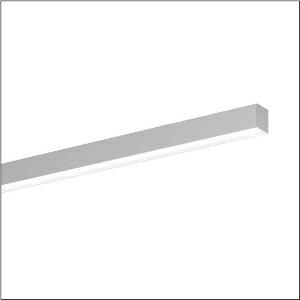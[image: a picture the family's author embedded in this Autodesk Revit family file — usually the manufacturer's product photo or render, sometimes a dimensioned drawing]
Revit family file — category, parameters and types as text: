
# Revit family: silica_r__21_51mx20tat2s_7558
name_source: partatom
category: Lighting Fixtures
units: mm (PartAtom-declared; Revit-internal decimal feet)

## family parameters
Cut with Voids When Loaded = No
Host = Face
Light Source = No
Part Type = Normal
Room Calculation Point = No
Round Connector Dimension = Use Diameter
Shared = No

## types (1)
- --- (1 x LED, 2400 lm, 20.5 W, 6500K)
    Apparent Load = 21 VA
    CIE Flux Codes = 48 79 96 100 100
    Color Rendering = 80
    Color Temperature = 6500K
    Default Elevation = 1800 mm
    Description = Silica® 21, office luminaire, primary optical cover: cover, of PMMA, opal, light emission: direct distribution, primary light characteristic: symmetric, installation type: surface-mounted, LED, rated luminous flux: 2.400lm, luminous efficacy: 112lm/W, light colour: 8tw, colour temperature: 2700..6500K, control gear: ECG DALI, with terminal, 3+2-pole, max. 2.5mm², mains connection: 220..240V, AC, 50/60Hz, rated input power: 21.5W, luminaire housing, of aluminium, metallic grey (RAL 9006), length: 1.204mm, width: 53mm, height: 53mm, protection rating (complete): IP20, insulation class (complete): insulation class I (protective earthing), certification: CE, permissible operating ambient temperature: 0..+35°C, standard: EN 50419, packaging unit: 1 piece
    Height = 0 mm  [stored 0 ft]
    Lamp = 1 x LED
    Lamp Light Flux = 2400 lm
    Lamp Power = 20.5 W
    Lamp count = 1
    Length = 1204 mm
    Luminous efficacy = 117 lm/W
    Manufacturer = Siteco
    ModVariant = No
    Model = 51MX20TAT2S
    Mounting Place = Ceiling
    Mounting Type = Recessed
    Number of Poles = 1
    OnlyDefault = Yes
    Power Factor = 1
    Product Name = Silica® 21
    Product group = office luminaire | ceiling recessed
    ProductGroupID = 401
    Protection Class = Protection class I
    Protection Degree = IP 20
    RLX_Detail_Level = 1
    RLX_Emergency_Light_Flux = 0 lm
    RLX_Emergency_Type = 0
    RLX_Emergency_Type_DB = No
    RlxData = <blob elided: 23257 chars, md5=fb43e829>
    Socket = socket
    Standby Power = 0 W
    System Light Flux = 2400 lm
    System Power = 21 W
    Type Comments = individual setting
    Type Image = l_1313588.jpg
    URL = http://relux.com
    VarID = @adj_089043
    Voltage = 0 V
    Weight = 0.00 kg
    Width = 53 mm

note: [stored X ft] marks values corroborated as IEEE doubles in the binary element streams (Revit-internal decimal feet)

## geometry (parser evidence)
native form markers: Blend x4, Sweep x10
no freeform markers — native parametric forms only
